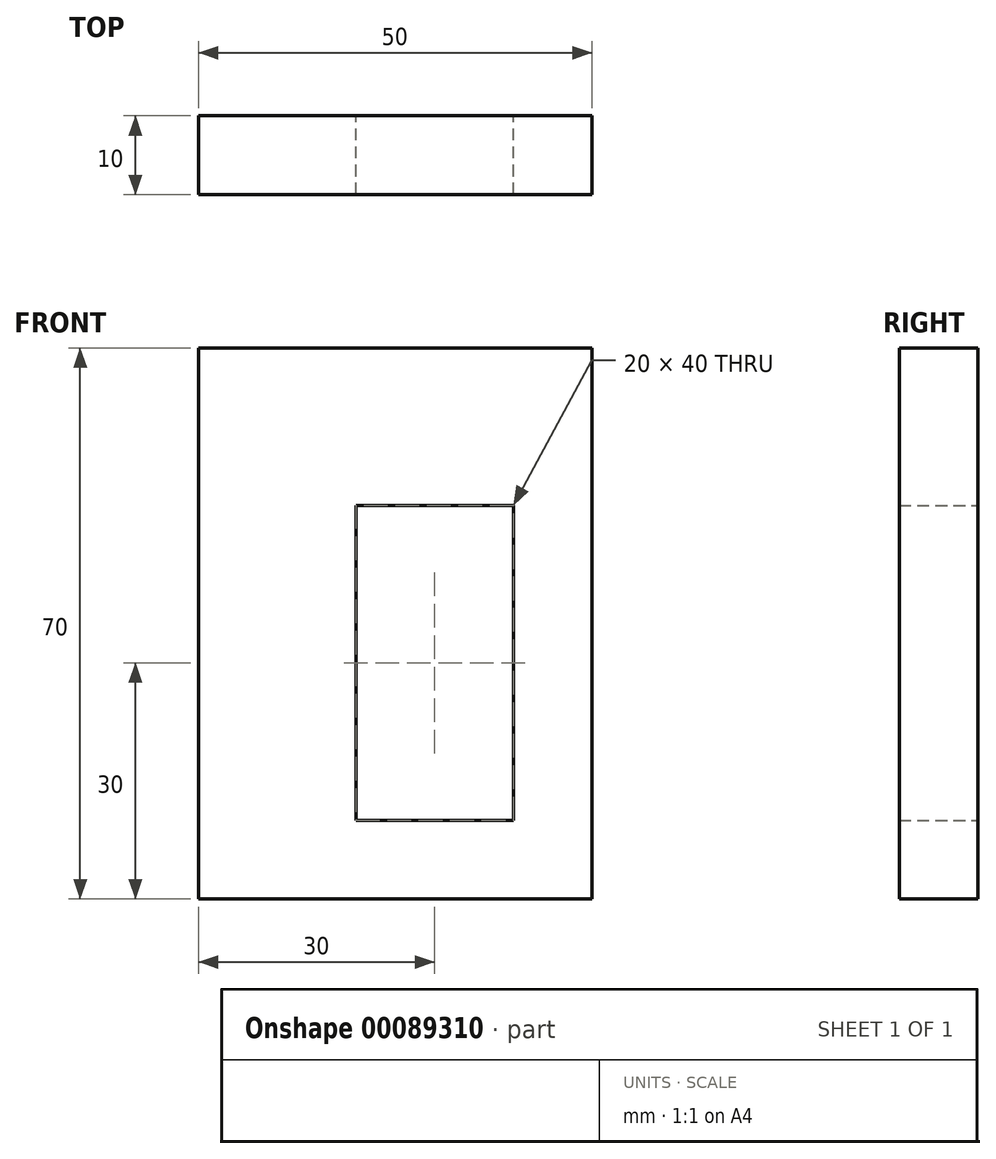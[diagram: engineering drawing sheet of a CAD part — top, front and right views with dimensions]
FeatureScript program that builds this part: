
annotation { "Feature Type Name" : "Feature", "Feature Type Description" : "" }
export const myFeature = defineFeature(function(context is Context, id is Id, definition is map)
    precondition{}
    {
        {
            var Q0;
            Q0=qCreatedBy(makeId("Front.planeOp"),FACE);
            var sketch = newSketch(context, id + "F0", { "sketchPlane" : qUnion([Q0])});
            skLineSegment(sketch, "E0.bottom", {"start": v(0, 0) * mm, "end": v(50, 0) * mm});
            skLineSegment(sketch, "E0.top", {"start": v(0, 70) * mm, "end": v(50, 70) * mm});
            skLineSegment(sketch, "E0.left", {"start": v(0, 0) * mm, "end": v(0, 70) * mm});
            skLineSegment(sketch, "E0.right", {"start": v(50, 0) * mm, "end": v(50, 70) * mm});
            skLineSegment(sketch, "E1.bottom", {"start": v(20, 10) * mm, "end": v(40, 10) * mm});
            skLineSegment(sketch, "E1.top", {"start": v(20, 50) * mm, "end": v(40, 50) * mm});
            skLineSegment(sketch, "E1.left", {"start": v(20, 10) * mm, "end": v(20, 50) * mm});
            skLineSegment(sketch, "E1.right", {"start": v(40, 10) * mm, "end": v(40, 50) * mm});
            skSolve(sketch);
        }
        {
            var Q0;
            Q0 = qSketchRegion(id + "F0", true);
            extrude(context, id + "F1", {"entities" : qUnion([Q0]), "depth" : 10 * mm});
        }
    });
